# Revit family: PROOX Circular waste chute EN
name_source: partatom
category: Möbel
revit_build: Autodesk Revit 2014 (Build: 20130308_1515(x64)
units: mm (PartAtom-declared; Revit-internal decimal feet)

## types (1)
- ONE pure
    BIM objects producer = www.BIMtelligent.eu
    Beschreibung = circular waste chute PROOX ONE made from stainless steel
    EAN-No. = 9120050350083
    Hersteller = PROOX Ltd.
    Kosten = 101 $
    Material = PROOX Stainless steel, brushed
    Modell = PU-280
    Product data sheet = http://www.proox.com
    Specification = Circular waste chute made out of stainless steel. For top or underneath mounting onto counters. Wire basket available as separate product. Incl. mounting clips and screws.
    Typenkommentare = ONE pure
    URL = http://www.proox.com
    Vorgabe-Ansicht = 0 mm  [stored 0 ft]

note: [stored X ft] marks values corroborated as IEEE doubles in the binary element streams (Revit-internal decimal feet)

## geometry (parser evidence)
native form markers: Sweep x1
no freeform markers — native parametric forms only
